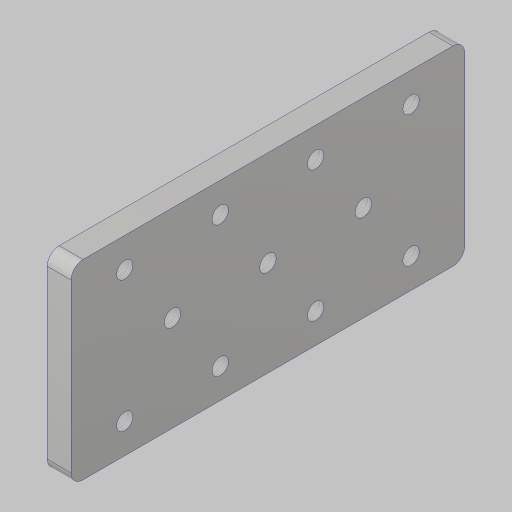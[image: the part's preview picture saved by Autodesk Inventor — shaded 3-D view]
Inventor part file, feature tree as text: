
AUTODESK INVENTOR PART (.ipt)
format: ipt  version: 2023.5 (Build 275446000, 446)  size: 140,800 bytes
history: native  units: in
note: dims shown in document units (in); Inventor stores cm internally (conversion verified against a paired STEP export)
features: sketch x2, extrude x1, hole x1, fillet x1, projected_geometry x1
ambient origin geometry x8: Origin, YZ Plane, XZ Plane, XY Plane, X Axis, Y Axis, Z Axis, Center Point
bodies: Solid1 (feature_tree)
feature tree (6):
  extrude  "Extrusion1"  Depth=2.0in
  hole  "Hole1"  [1 undecoded]
  fillet  "Fillet1"  Radius=0.5625in
  sketch  "Sketch1"  dims[d0=4.125in d1=2.0in]
  sketch  "Sketch2"  dims[d2=0.25in d3=0.5in d4=0.0in d5=0.0in d6=1.375in d7=0.5625in d8=0.5in d9=1.5748in d11=1.0in d12=0.3937in d14=1.0in d16=0.171in d17=0.432in d18=0.385in d19=0.25in d20=0.5635in d21=1.0in d22=0.8108in d23=0.125in]
  projected_geometry  "Project Cut Edges1"
note: 1 required parameter value undecoded (feature->parameter linkage not recoverable at this tier; creation-order binding heuristic only, values carry confidence <= 0.55)
